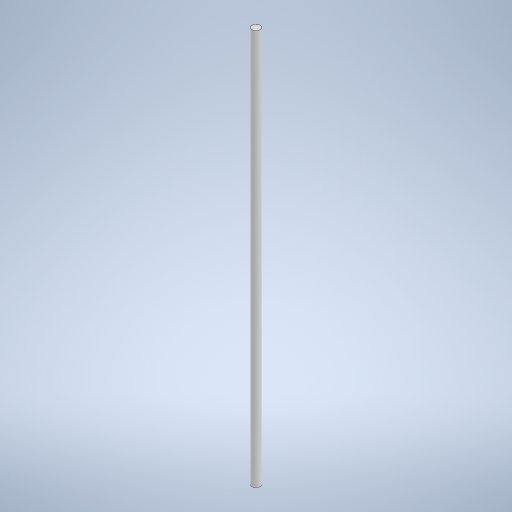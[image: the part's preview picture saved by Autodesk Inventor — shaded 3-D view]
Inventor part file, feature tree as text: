
AUTODESK INVENTOR PART (.ipt)
format: ipt  version: 2024 (Build 280153000, 153)  size: 230,400 bytes
history: native  units: mm
features: extrude x1, sketch x1
ambient origin geometry x8: Origin, YZ Plane, XZ Plane, XY Plane, X Axis, Y Axis, Z Axis, Center Point
bodies: Volumenkörper1 (feature_tree)
feature tree (2):
  extrude  "Extrusion1"  Depth=300.0mm TaperAngle=0.0deg
  sketch  "Skizze1"  dims[d0=6.0mm d1=300.0mm d2=0.0mm]
